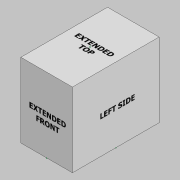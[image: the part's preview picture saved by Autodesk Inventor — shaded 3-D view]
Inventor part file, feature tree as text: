
AUTODESK INVENTOR PART (.ipt)
format: ipt  version: 2021 (Build 250183000, 183)  size: 91,136 bytes
history: native  units: mm
features: sketch x7, extrude x1
ambient origin geometry x8: Origin, YZ Plane, XZ Plane, XY Plane, X Axis, Y Axis, Z Axis, Center Point
bodies: Solid1 (feature_tree)
feature tree (8):
  extrude  "Extrusion1"  Depth=106.7mm
  sketch  "Sketch2"  dims[d2=53.35mm]
  sketch  "Sketch3"  dims[d3=31.75mm]
  sketch  "Sketch4"  dims[d4=91.4mm]
  sketch  "Sketch5"  dims[d5=0.0mm]
  sketch  "Sketch6"
  sketch  "Sketch7"
  sketch  "Sketch1"  dims[d0=63.5mm d1=106.7mm]
